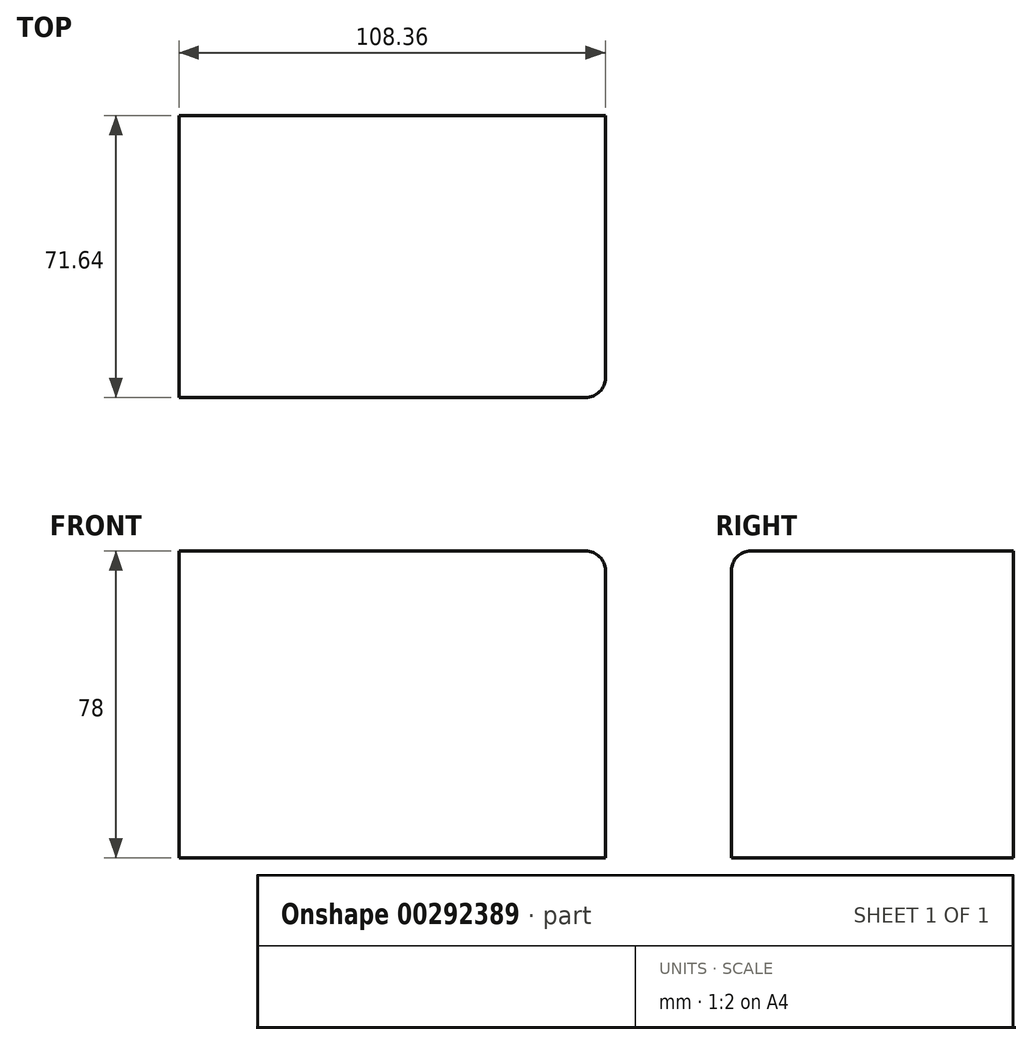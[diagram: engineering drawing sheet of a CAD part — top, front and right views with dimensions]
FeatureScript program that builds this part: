
annotation { "Feature Type Name" : "Feature", "Feature Type Description" : "" }
export const myFeature = defineFeature(function(context is Context, id is Id, definition is map)
    precondition{}
    {
        {
            var Q0;
            Q0=qCreatedBy(makeId("Top.planeOp"),FACE);
            var sketch = newSketch(context, id + "F0", { "sketchPlane" : qUnion([Q0])});
            skLineSegment(sketch, "E0.bottom", {"start": v(54.18, 35.82) * mm, "end": v(-54.18, 35.82) * mm});
            skLineSegment(sketch, "E0.top", {"start": v(54.18, -35.82) * mm, "end": v(-54.18, -35.82) * mm});
            skLineSegment(sketch, "E0.left", {"start": v(54.18, 35.82) * mm, "end": v(54.18, -35.82) * mm});
            skLineSegment(sketch, "E0.right", {"start": v(-54.18, 35.82) * mm, "end": v(-54.18, -35.82) * mm});
            skPoint(sketch, "E0.middle", {"position": v(0, 0) * mm});
            skSolve(sketch);
        }
        {
            var Q0;
            Q0=makeQuery(id+"F0.imprint","IMPRINT",FACE,{"disambiguationData":[TD([[makeQuery(id+"F0.imprint","IMPRINT",EDGE,{"derivedFrom":sQuery(id+"F0.wireOp",EDGE,"E0.bottom")}),1.0]])]});
            extrude(context, id + "F1", {"entities" : qUnion([Q0]), "depth" : 78 * mm});
        }
        {
            var Q0;
            Q0=makeQuery(id+"F1.opExtrude","CAP_EDGE",EDGE,{"disambiguationData":[OSD([sQuery(id+"F0.wireOp",EDGE,"E0.top")])],"isStart":false});
            var Q1;
            Q1=makeQuery(id+"F1.opExtrude","CAP_EDGE",EDGE,{"disambiguationData":[OSD([sQuery(id+"F0.wireOp",EDGE,"E0.left")])],"isStart":false});
            var Q2;
            Q2=makeQuery(id+"F1.opExtrude","SWEPT_EDGE",EDGE,{"disambiguationData":[OSD([sQuery(id+"F0.wireOp",EDGE,"E0.top"),sQuery(id+"F0.wireOp",EDGE,"E0.left")])]});
            fillet(context, id + "F2", {"entities" : qUnion([Q0, Q1, Q2]), "radius" : 5 * mm, "tangentPropagation" : true, "allowEdgeOverflow" : false});
        }
    });
